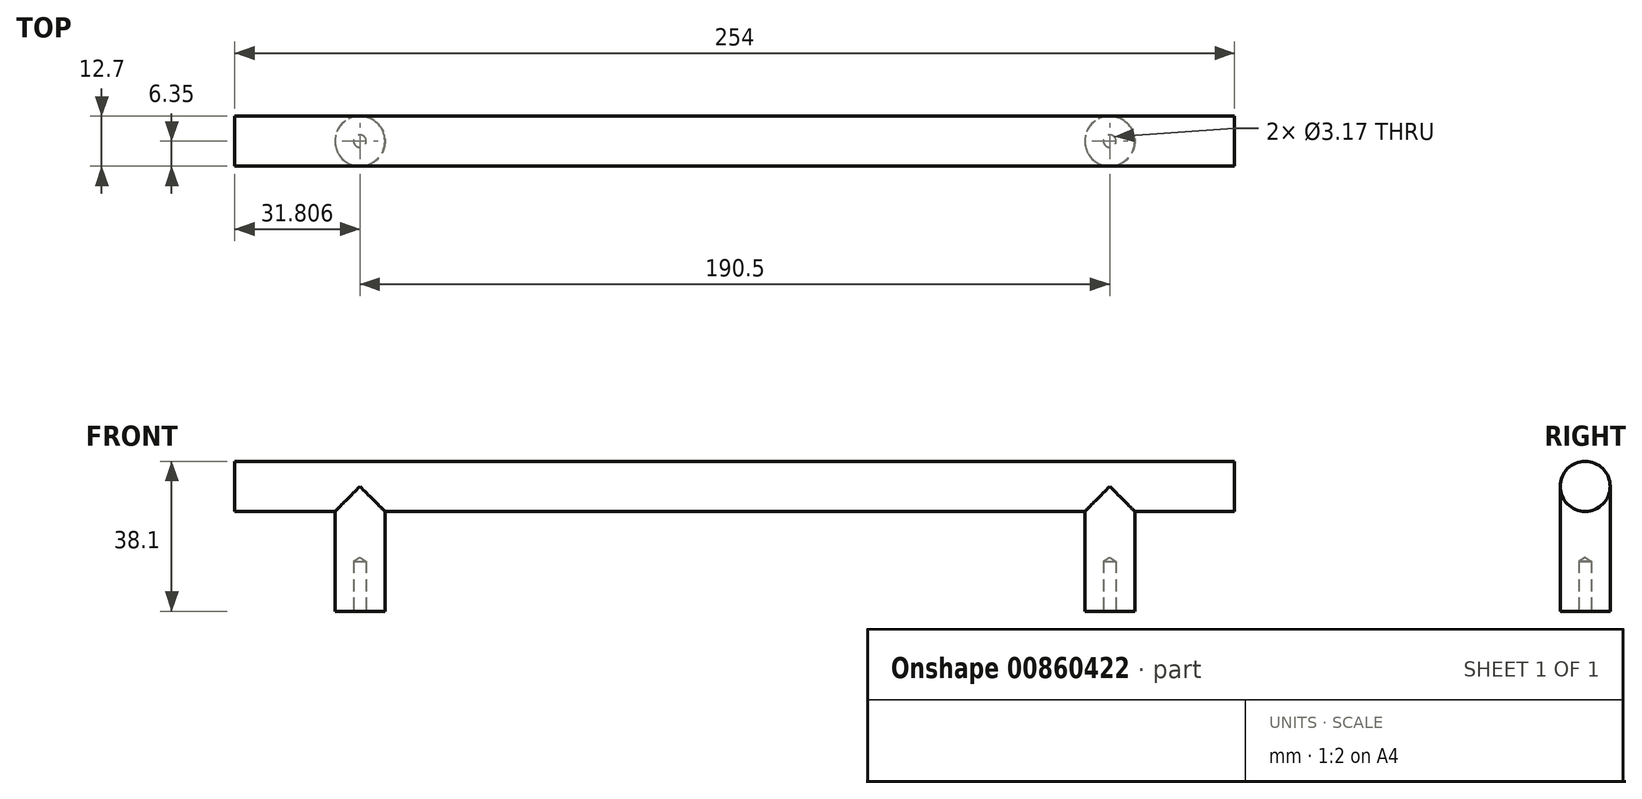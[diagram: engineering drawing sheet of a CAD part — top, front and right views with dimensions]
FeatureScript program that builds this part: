
annotation { "Feature Type Name" : "Feature", "Feature Type Description" : "" }
export const myFeature = defineFeature(function(context is Context, id is Id, definition is map)
    precondition{}
    {
        {
            var Q0;
            Q0=qCreatedBy(makeId("Front.planeOp"),FACE);
            var sketch = newSketch(context, id + "F0", { "sketchPlane" : qUnion([Q0])});
            skLineSegment(sketch, "E0", {"start": v(0, 0) * mm, "end": v(-254, 0) * mm});
            skLineSegment(sketch, "E1", {"start": v(-31.75, 0) * mm, "end": v(-31.75, -31.75) * mm});
            skLineSegment(sketch, "E2", {"start": v(-127, 0) * mm, "end": v(-127, -19.72) * mm, "construction": true});
            skLineSegment(sketch, "E3.MirrorCS", {"start": v(-222.25, 0) * mm, "end": v(-222.25, -31.75) * mm});
            skSolve(sketch);
        }
        {
            var Q0;
            Q0=qCreatedBy(makeId("Right.planeOp"),FACE);
            var sketch = newSketch(context, id + "F1", { "sketchPlane" : qUnion([Q0])});
            skCircle(sketch, "E4", {"center": v(0, 0) * mm, "radius": 6.35 * mm});
            skSolve(sketch);
        }
        {
            var Q0;
            Q0=makeQuery(id+"F1.imprint","IMPRINT",FACE,{"disambiguationData":[TD([[makeQuery(id+"F1.imprint","IMPRINT",EDGE,{"derivedFrom":sQuery(id+"F1.wireOp",EDGE,"E4")}),1.0]])]});
            var Q1;
            Q1=sQuery(id+"F0.wireOp",EDGE,"E0");
            sweep(context, id + "F2", {"profiles" : qUnion([Q0]), "path" : qUnion([Q1])});
        }
        {
            var Q0;
            Q0=qCreatedBy(makeId("Top.planeOp"),FACE);
            var sketch = newSketch(context, id + "F3", { "sketchPlane" : qUnion([Q0])});
            skCircle(sketch, "E5", {"center": v(-222.2, 0) * mm, "radius": 6.35 * mm});
            skCircle(sketch, "E6", {"center": v(-31.7, 0) * mm, "radius": 6.35 * mm});
            skSolve(sketch);
        }
        {
            var Q0;
            Q0 = qSketchRegion(id + "F3", true);
            var Q1;
            Q1=sQuery(id+"F0.wireOp",EDGE,"E3.MirrorCS");
            sweep(context, id + "F4", {"operationType" : NewBodyOperationType.ADD, "profiles" : qUnion([Q0]), "path" : qUnion([Q1])});
        }
        {
            var Q0;
            Q0=makeQuery(id+"F4.opSweep","CAP_FACE",FACE,{"disambiguationData":[OSD([sQuery(id+"F0.wireOp",VERTEX,"E3.MirrorCS.end"),sQuery(id+"F3.wireOp",EDGE,"E5")])],"isStart":false});
            var sketch = newSketch(context, id + "F5", { "sketchPlane" : qUnion([Q0])});
            skPoint(sketch, "E7", {"position": v(-222.2, 0) * mm});
            skPoint(sketch, "E8", {"position": v(-31.7, 0) * mm});
            skSolve(sketch);
        }
        {
            var Q0;
            Q0=sQuery(id+"F5.wireOp",VERTEX,"E7");
            var Q1;
            Q1=sQuery(id+"F5.wireOp",VERTEX,"E8");
            var Q2;
            Q2=makeQuery(id+"F2.opSweep","SWEPT_BODY",BODY,{"disambiguationData":[OSD([sQuery(id+"F0.wireOp",EDGE,"E0"),sQuery(id+"F1.wireOp",EDGE,"E4")])]});
            hole(context, id + "F6", {"style" : HoleStyle.SIMPLE, "endStyle" : HoleEndStyle.BLIND, "holeDiameter" : 3.17 * mm, "majorDiameter" : 6.35 * mm, "holeDepth" : 12.7 * mm, "isTappedThrough" : true, "tappedDepth" : 12.7 * mm, "tapClearance" : 3, "locations" : qUnion([Q0, Q1]), "scope" : qUnion([Q2])});
        }
    });
